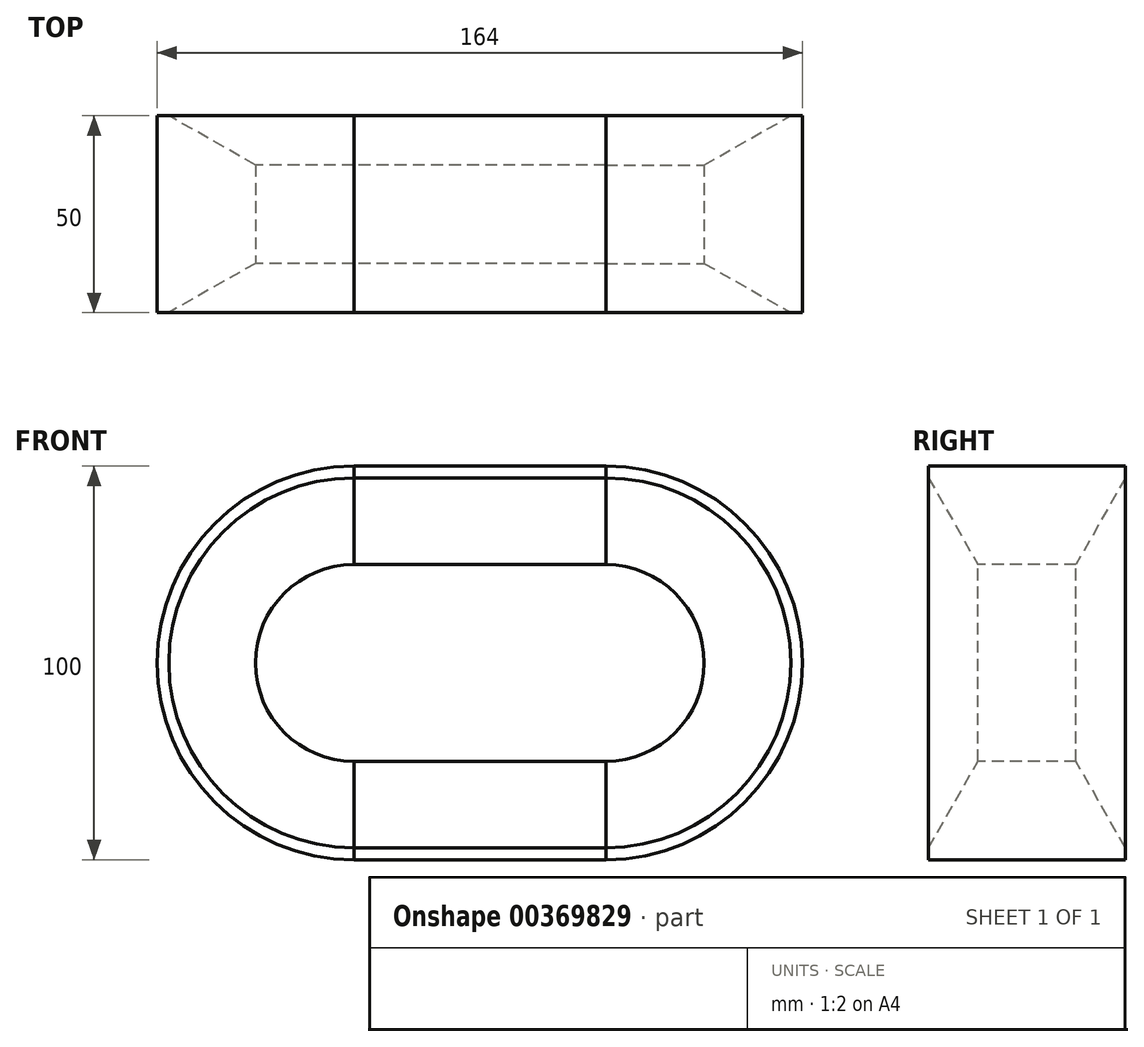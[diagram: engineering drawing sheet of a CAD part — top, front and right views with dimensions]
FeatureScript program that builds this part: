
annotation { "Feature Type Name" : "Feature", "Feature Type Description" : "" }
export const myFeature = defineFeature(function(context is Context, id is Id, definition is map)
    precondition{}
    {
        {
            var Q0;
            Q0=qCreatedBy(makeId("Right.planeOp"),FACE);
            var sketch = newSketch(context, id + "F0", { "sketchPlane" : qUnion([Q0])});
            skLineSegment(sketch, "E0", {"start": v(0, 0) * mm, "end": v(0, 3) * mm});
            skLineSegment(sketch, "E1", {"start": v(50, 3) * mm, "end": v(50, 0) * mm});
            skLineSegment(sketch, "E2", {"start": v(50, 0) * mm, "end": v(0, 0) * mm});
            skLineSegment(sketch, "E3", {"start": v(50, 3) * mm, "end": v(37.5, 25) * mm});
            skLineSegment(sketch, "E4", {"start": v(0, 3) * mm, "end": v(12.5, 25) * mm});
            skLineSegment(sketch, "E5", {"start": v(12.5, 25) * mm, "end": v(25, 50) * mm});
            skLineSegment(sketch, "E6", {"start": v(25, 50) * mm, "end": v(37.5, 25) * mm});
            skSolve(sketch);
        }
        {
            var Q0;
            Q0=makeQuery(id+"F0.imprint","IMPRINT",FACE,{"disambiguationData":[TD([[makeQuery(id+"F0.imprint","IMPRINT",EDGE,{"derivedFrom":sQuery(id+"F0.wireOp",EDGE,"E0")}),-1.0]])]});
            extrude(context, id + "F1", {"entities" : qUnion([Q0]), "depth" : 64 * mm});
        }
        {
            var Q0;
            Q0=makeQuery(id+"F1.opExtrude","SWEPT_EDGE",EDGE,{"disambiguationData":[OSD([sQuery(id+"F0.wireOp",EDGE,"E5"),sQuery(id+"F0.wireOp",EDGE,"E6")])]});
            cPlane(context, id + "F2", {"entities" : qUnion([Q0]), "cplaneType" : CPlaneType.LINE_ANGLE, "offset" : 0 * mm, "angle" : 90 * degree, "flipAlignment" : true, "width" : 150 * mm, "height" : 150 * mm});
        }
        {
            var Q0;
            Q0=makeQuery(id+"F1.opExtrude","SWEPT_BODY",BODY,{"disambiguationData":[OSD([sQuery(id+"F0.wireOp",EDGE,"E0"),sQuery(id+"F0.wireOp",EDGE,"E1"),sQuery(id+"F0.wireOp",EDGE,"E2"),sQuery(id+"F0.wireOp",EDGE,"E3"),sQuery(id+"F0.wireOp",EDGE,"E4"),sQuery(id+"F0.wireOp",EDGE,"E5"),sQuery(id+"F0.wireOp",EDGE,"E6")])]});
            var Q1;
            Q1=qCreatedBy(id+"F2.planeOp",FACE);
            mirror(context, id + "F3", {"entities" : qUnion([Q0]), "mirrorPlane" : qUnion([Q1])});
        }
        {
            var Q0;
            Q0=qCreatedBy(id+"F2.planeOp",FACE);
            var sketch = newSketch(context, id + "F4", { "sketchPlane" : qUnion([Q0])});
            skLineSegment(sketch, "E7", {"start": v(0, 0) * mm, "end": v(0, 50) * mm});
            skLineSegment(sketch, "E8", {"start": v(0, 50) * mm, "end": v(64, 50) * mm});
            skLineSegment(sketch, "E9", {"start": v(64, 50) * mm, "end": v(64, 0) * mm});
            skLineSegment(sketch, "E10", {"start": v(64, 0) * mm, "end": v(0, 0) * mm});
            skSolve(sketch);
        }
        {
            var Q0;
            Q0=makeQuery(id+"F3.opPattern","COPY",FACE,{"derivedFrom":makeQuery(id+"F1.opExtrude","CAP_FACE",FACE,{"disambiguationData":[OSD([sQuery(id+"F0.wireOp",EDGE,"E0"),sQuery(id+"F0.wireOp",EDGE,"E1"),sQuery(id+"F0.wireOp",EDGE,"E2"),sQuery(id+"F0.wireOp",EDGE,"E3"),sQuery(id+"F0.wireOp",EDGE,"E4"),sQuery(id+"F0.wireOp",EDGE,"E5"),sQuery(id+"F0.wireOp",EDGE,"E6")])],"isStart":false}),"instanceName":"1"});
            var Q1;
            Q1=sQuery(id+"F4.wireOp",EDGE,"E9");
            revolve(context, id + "F5", {"entities" : qUnion([Q0]), "axis" : qUnion([Q1]), "revolveType" : RevolveType.ONE_DIRECTION, "oppositeDirection" : true, "angle" : 180 * degree});
        }
        {
            var Q0;
            Q0=makeQuery(id+"F3.opPattern","COPY",FACE,{"derivedFrom":makeQuery(id+"F1.opExtrude","CAP_FACE",FACE,{"disambiguationData":[OSD([sQuery(id+"F0.wireOp",EDGE,"E0"),sQuery(id+"F0.wireOp",EDGE,"E1"),sQuery(id+"F0.wireOp",EDGE,"E2"),sQuery(id+"F0.wireOp",EDGE,"E3"),sQuery(id+"F0.wireOp",EDGE,"E4"),sQuery(id+"F0.wireOp",EDGE,"E5"),sQuery(id+"F0.wireOp",EDGE,"E6")])],"isStart":true}),"instanceName":"1"});
            cPlane(context, id + "F6", {"entities" : qUnion([Q0]), "cplaneType" : CPlaneType.OFFSET, "offset" : 32 * mm, "oppositeDirection" : true, "width" : 150 * mm, "height" : 150 * mm});
        }
        {
            var Q0;
            Q0=makeQuery(id+"F5.opRevolve","SWEPT_BODY",BODY,{"disambiguationData":[OSD([sQuery(id+"F0.wireOp",EDGE,"E0"),sQuery(id+"F0.wireOp",EDGE,"E1"),sQuery(id+"F0.wireOp",EDGE,"E2"),sQuery(id+"F0.wireOp",EDGE,"E3"),sQuery(id+"F0.wireOp",EDGE,"E4"),sQuery(id+"F0.wireOp",EDGE,"E5"),sQuery(id+"F0.wireOp",EDGE,"E6")])]});
            var Q1;
            Q1=qCreatedBy(id+"F6.planeOp",FACE);
            mirror(context, id + "F7", {"entities" : qUnion([Q0]), "mirrorPlane" : qUnion([Q1])});
        }
        {
            var Q0;
            Q0=qCreatedBy(makeId("Front.planeOp"),FACE);
            var sketch = newSketch(context, id + "F8", { "sketchPlane" : qUnion([Q0])});
            skLineSegment(sketch, "E11", {"start": v(0, 75) * mm, "end": v(64, 75) * mm});
            skLineSegment(sketch, "E12", {"start": v(64, 25) * mm, "end": v(0, 25) * mm});
            skArc(sketch, "E13", {"start": v(0, 75) * mm, "mid": v(-25, 50) * mm, "end": v(0, 25) * mm});
            skArc(sketch, "E14", {"start": v(64, 25) * mm, "mid": v(89, 50) * mm, "end": v(64, 75) * mm});
            skSolve(sketch);
        }
        {
            var Q0;
            Q0 = qSketchRegion(id + "F8", true);
            extrude(context, id + "F9", {"entities" : qUnion([Q0]), "operationType" : NewBodyOperationType.REMOVE, "endBound" : BoundingType.SYMMETRIC, "oppositeDirection" : true, "depth" : 118 * mm});
        }
    });
